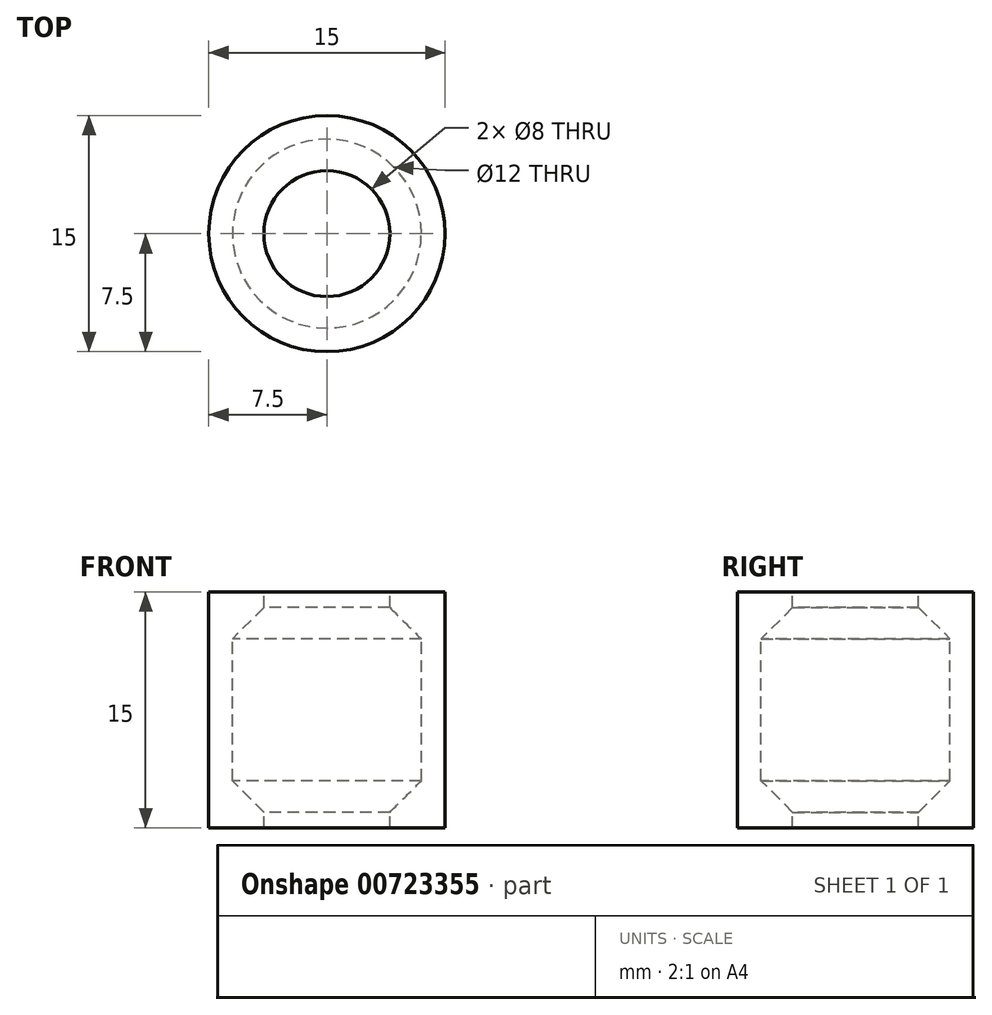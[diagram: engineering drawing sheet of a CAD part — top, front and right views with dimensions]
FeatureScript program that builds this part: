
annotation { "Feature Type Name" : "Feature", "Feature Type Description" : "" }
export const myFeature = defineFeature(function(context is Context, id is Id, definition is map)
    precondition{}
    {
        {
            var Q0;
            Q0=qCreatedBy(makeId("Top.planeOp"),FACE);
            var sketch = newSketch(context, id + "F0", { "sketchPlane" : qUnion([Q0])});
            skCircle(sketch, "E0", {"center": v(0, 0) * mm, "radius": 7.5 * mm});
            skCircle(sketch, "E1", {"center": v(0, 0) * mm, "radius": 4 * mm});
            skSolve(sketch);
        }
        {
            var Q0;
            Q0=qCreatedBy(makeId("Top.planeOp"),FACE);
            cPlane(context, id + "F1", {"entities" : qUnion([Q0]), "cplaneType" : CPlaneType.OFFSET, "offset" : 3 * mm, "oppositeDirection" : true, "width" : 150 * mm, "height" : 150 * mm});
        }
        {
            var Q0;
            Q0=makeQuery(id+"F0.imprint","IMPRINT",FACE,{"disambiguationData":[TD([[makeQuery(id+"F0.imprint","IMPRINT",EDGE,{"derivedFrom":sQuery(id+"F0.wireOp",EDGE,"E0")}),1.0]])]});
            extrude(context, id + "F2", {"entities" : qUnion([Q0]), "oppositeDirection" : true, "depth" : 15 * mm, "offsetDistance" : 25 * mm});
        }
        {
            var Q0;
            Q0=qCreatedBy(id+"F1.planeOp",FACE);
            var sketch = newSketch(context, id + "F3", { "sketchPlane" : qUnion([Q0])});
            skCircle(sketch, "E2", {"center": v(0, 0) * mm, "radius": 6 * mm});
            skSolve(sketch);
        }
        {
            var Q0;
            Q0 = qSketchRegion(id + "F3", true);
            extrude(context, id + "F4", {"entities" : qUnion([Q0]), "operationType" : NewBodyOperationType.REMOVE, "oppositeDirection" : true, "depth" : 9 * mm, "offsetDistance" : 25 * mm});
        }
        {
            var Q0;
            Q0=makeQuery(id+"F4.boolean.opBoolean","INTERSECT",EDGE,{"derivedFrom":[makeQuery(id+"F2.opExtrude","SWEPT_FACE",FACE,{"disambiguationData":[OSD([sQuery(id+"F0.wireOp",EDGE,"E1")])]}),makeQuery(id+"F4.opExtrude","CAP_FACE",FACE,{"disambiguationData":[OSD([sQuery(id+"F3.wireOp",EDGE,"E2")])],"isStart":true})]});
            var Q1;
            Q1=makeQuery(id+"F4.boolean.opBoolean","INTERSECT",EDGE,{"derivedFrom":[makeQuery(id+"F2.opExtrude","SWEPT_FACE",FACE,{"disambiguationData":[OSD([sQuery(id+"F0.wireOp",EDGE,"E1")])]}),makeQuery(id+"F4.opExtrude","CAP_FACE",FACE,{"disambiguationData":[OSD([sQuery(id+"F3.wireOp",EDGE,"E2")])],"isStart":false})]});
            chamfer(context, id + "F5", {"entities" : qUnion([Q0, Q1]), "width" : 2 * mm, "tangentPropagation" : true});
        }
    });
